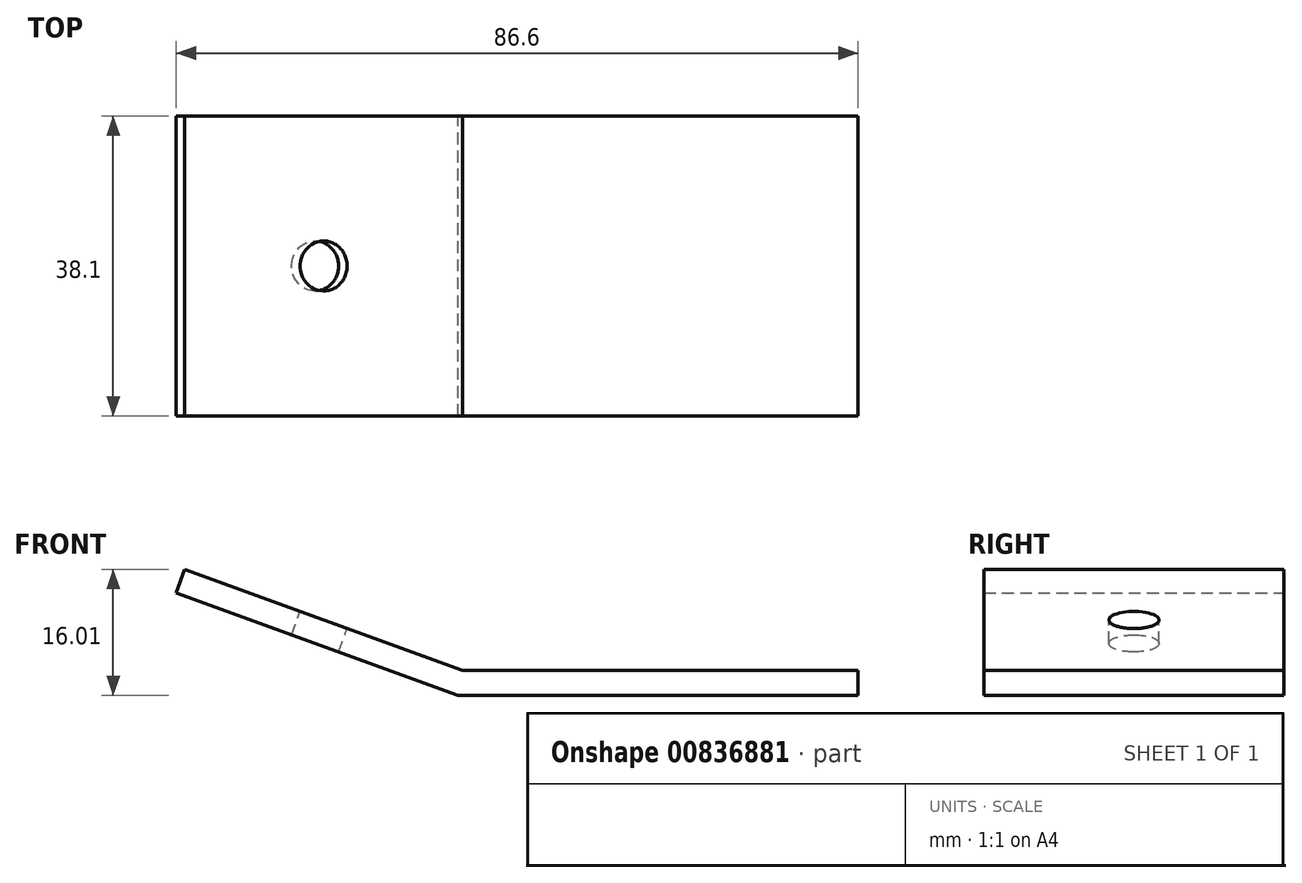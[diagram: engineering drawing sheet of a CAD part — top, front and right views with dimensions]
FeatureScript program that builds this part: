
annotation { "Feature Type Name" : "Feature", "Feature Type Description" : "" }
export const myFeature = defineFeature(function(context is Context, id is Id, definition is map)
    precondition{}
    {
        {
            var Q0;
            Q0=qCreatedBy(makeId("Front.planeOp"),FACE);
            var sketch = newSketch(context, id + "F0", { "sketchPlane" : qUnion([Q0])});
            skLineSegment(sketch, "E0", {"start": v(3.82, 0) * mm, "end": v(-31.98, 13.03) * mm});
            skLineSegment(sketch, "E1", {"start": v(3.82, 0) * mm, "end": v(54.62, 0) * mm});
            skLineSegment(sketch, "E2", {"start": v(54.62, 0) * mm, "end": v(54.62, 3.18) * mm});
            skLineSegment(sketch, "E3", {"start": v(54.62, 3.18) * mm, "end": v(4.38, 3.17) * mm});
            skLineSegment(sketch, "E4", {"start": v(4.38, 3.17) * mm, "end": v(-30.9, 16.01) * mm});
            skLineSegment(sketch, "E5", {"start": v(-30.9, 16.01) * mm, "end": v(-31.98, 13.03) * mm});
            skSolve(sketch);
        }
        {
            var Q0;
            Q0=makeQuery(id+"F0.imprint","IMPRINT",FACE,{"disambiguationData":[TD([[makeQuery(id+"F0.imprint","IMPRINT",EDGE,{"derivedFrom":sQuery(id+"F0.wireOp",EDGE,"E0")}),-1.0]])]});
            extrude(context, id + "F1", {"entities" : qUnion([Q0]), "depth" : 38.1 * mm, "offsetDistance" : 25.4 * mm});
        }
        {
            var Q0;
            Q0=makeQuery(id+"F1.opExtrude","SWEPT_FACE",FACE,{"disambiguationData":[OSD([sQuery(id+"F0.wireOp",EDGE,"E4")])]});
            var sketch = newSketch(context, id + "F2", { "sketchPlane" : qUnion([Q0])});
            skCircle(sketch, "E6", {"center": v(-15.74, -19.05) * mm, "radius": 3.18 * mm});
            skPoint(sketch, "E6.centerSnap0", {"position": v(-15.74, 0) * mm});
            skPoint(sketch, "E6.centerSnap1", {"position": v(-34.51, -19.05) * mm});
            skSolve(sketch);
        }
        {
            var Q0;
            Q0=makeQuery(id+"F2.imprint","IMPRINT",FACE,{"disambiguationData":[TD([[makeQuery(id+"F2.imprint","IMPRINT",EDGE,{"derivedFrom":sQuery(id+"F2.wireOp",EDGE,"E6")}),1.0]])]});
            extrude(context, id + "F3", {"entities" : qUnion([Q0]), "operationType" : NewBodyOperationType.REMOVE, "oppositeDirection" : true, "depth" : 25.4 * mm, "offsetDistance" : 25.4 * mm});
        }
    });
